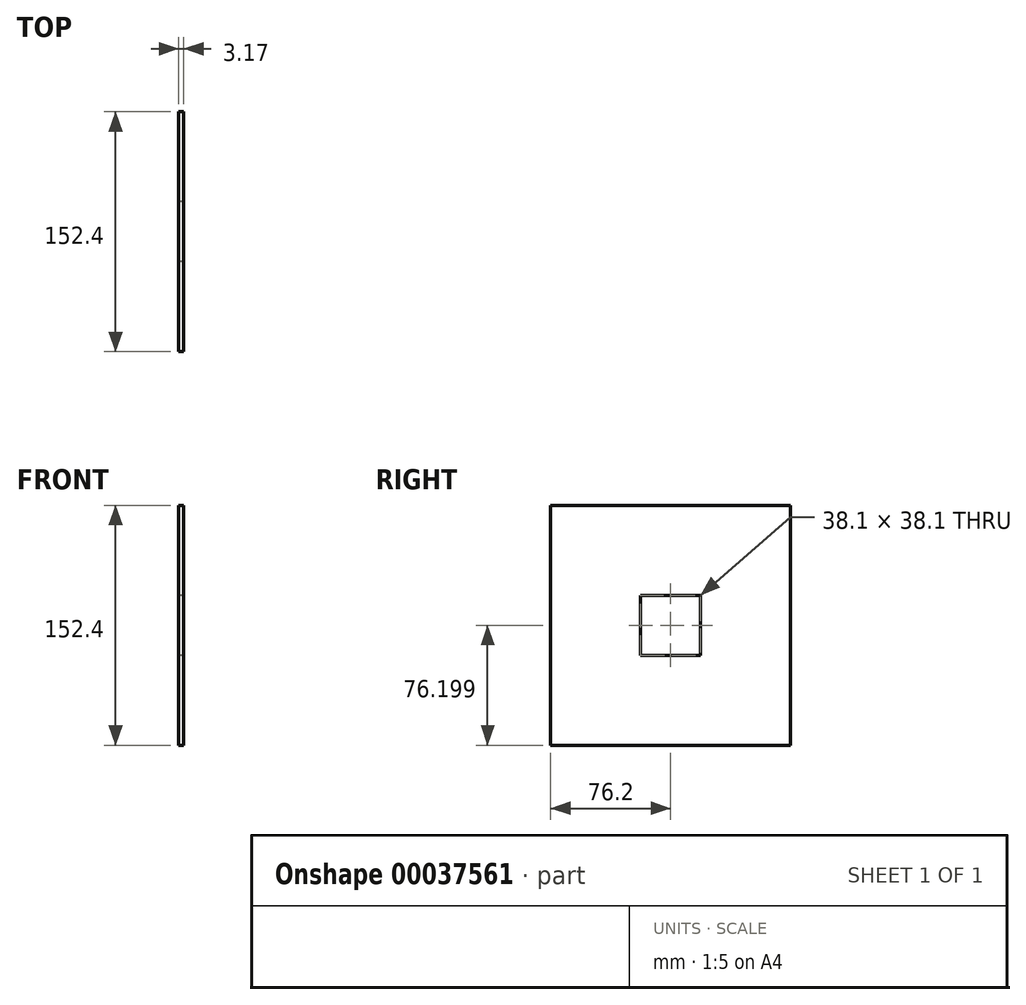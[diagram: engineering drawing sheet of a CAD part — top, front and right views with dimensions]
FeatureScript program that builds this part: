
annotation { "Feature Type Name" : "Feature", "Feature Type Description" : "" }
export const myFeature = defineFeature(function(context is Context, id is Id, definition is map)
    precondition{}
    {
        {
            var Q0;
            Q0=qCreatedBy(makeId("Right.planeOp"),FACE);
            var sketch = newSketch(context, id + "F0", { "sketchPlane" : qUnion([Q0])});
            skLineSegment(sketch, "E0.rect.bottom", {"start": v(76.2, -68) * mm, "end": v(-76.2, -68) * mm});
            skLineSegment(sketch, "E0.rect.top", {"start": v(76.2, 84.4) * mm, "end": v(-76.2, 84.4) * mm});
            skLineSegment(sketch, "E0.rect.left", {"start": v(76.2, -68) * mm, "end": v(76.2, 84.4) * mm});
            skLineSegment(sketch, "E0.rect.right", {"start": v(-76.2, -68) * mm, "end": v(-76.2, 84.4) * mm});
            skPoint(sketch, "E0.rect.middle", {"position": v(0, 8.2) * mm});
            skLineSegment(sketch, "E1.rect.bottom", {"start": v(19.05, -10.85) * mm, "end": v(-19.05, -10.85) * mm});
            skLineSegment(sketch, "E1.rect.top", {"start": v(19.05, 27.25) * mm, "end": v(-19.05, 27.25) * mm});
            skLineSegment(sketch, "E1.rect.left", {"start": v(19.05, -10.85) * mm, "end": v(19.05, 27.25) * mm});
            skLineSegment(sketch, "E1.rect.right", {"start": v(-19.05, -10.85) * mm, "end": v(-19.05, 27.25) * mm});
            skSolve(sketch);
        }
        {
            var Q0;
            Q0=makeQuery(id+"F0.imprint","IMPRINT",FACE,{"disambiguationData":[TD([[makeQuery(id+"F0.imprint","IMPRINT",EDGE,{"derivedFrom":sQuery(id+"F0.wireOp",EDGE,"E0.rect.bottom")}),-1.0]])]});
            extrude(context, id + "F1", {"entities" : qUnion([Q0]), "depth" : 3.17 * mm});
        }
    });
